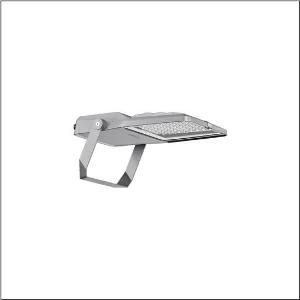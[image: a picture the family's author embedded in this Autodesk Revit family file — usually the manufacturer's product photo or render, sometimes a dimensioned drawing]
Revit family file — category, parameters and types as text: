
# Revit family: floodlight_fl_21_mini___pl33t_5xa7775c2f1a_de84
name_source: partatom
category: Lighting Fixtures
units: mm (PartAtom-declared; Revit-internal decimal feet)

## family parameters
Cut with Voids When Loaded = No
Host = Face
Light Source = No
Part Type = Normal
Room Calculation Point = No
Round Connector Dimension = Use Diameter
Shared = No

## types (1)
- --- (1 x LED, 12050 lm, 89 W, 3000K)
    Apparent Load = 89 VA
    CIE Flux Codes = 26 75 99 100 100
    Color Rendering = 70
    Color Temperature = 3000K
    Default Elevation = 1800 mm
    Description = Floodlight FL 21 mini, floodlight, primary light control with lens, of PMMA, primary optical cover: protective disc, of toughened safety glass, transparent, light distribution: PL33T, light emission: direct distribution, installation type: surface-mounted, LED, High Power LED, rated luminous flux: 12.050lm, luminous efficacy: 135lm/W, light colour: 730, colour temperature: 3000K, control: flexible luminous flux parameterisation, time-dependent luminous flux control, constant luminous flux control, overheat protection, presetting dimming logarithmic, with terminal, 6-pole, mains connection: 220..240V, AC, 50/60Hz, start of lifetime: 89W, end of service life: 94W, reduction: 43W, luminaire housing, of diecast aluminium, powder-coated, Siteco® metallic grey (DB 702S), corrosivity category C5 mid according to DIN EN ISO 12944, sealing non-destructively replaceable, mounting bracket, of steel, galvanised, powder-coated, Siteco® metallic grey (DB 702S), Smart Interface above, protection rating (complete): IP66, insulation class (complete): insulation class II (safety insulation), certification: CE, ENEC, VDE, protection symbol: D, impact resistance: IK08, permissible operating ambient temperature: -40..+40°C, permissible operating ambient temperature for outdoor applications: -40..+50°C, standard: DIN EN 12944, LABS conformity tested according to VDMA 24364:2018-05, packaging unit: 1 piece

Light Distribution: PL33T
    Height = 70 mm
    Lamp = 1 x LED
    Lamp Light Flux = 12050 lm
    Lamp Power = 89 W
    Lamp count = 1
    Length = 485 mm
    Luminous efficacy = 135 lm/W
    Manufacturer = Siteco
    ModVariant = No
    Model = 5XA7775C2F1A
    Number of Poles = 1
    OnlyDefault = Yes
    Power Factor = 1
    Product Name = Floodlight FL 21 mini | PL33T
    Product group = floodlight | pylon annexe
    ProductGroupID = 6200
    Protection Class = Protection class II
    Protection Degree = IP 66
    RLX_Detail_Level = 1
    RLX_Emergency_Light_Flux = 0 lm
    RLX_Emergency_Type = 0
    RLX_Emergency_Type_DB = No
    RlxData = <blob elided: 95901 chars, md5=86abb09b>
    Socket = socket
    Standby Power = 0 W
    System Light Flux = 12050 lm
    System Power = 89 W
    Type Comments = factory setting: luminous flux: 100 % | dim-lin: 254 | 456 mA
    Type Image = l_1006845.jpg
    URL = http://relux.com
    VarID = @adj_081057
    Voltage = 0 V
    Weight = 0.00 kg
    Width = 337 mm

## geometry (parser evidence)
native form markers: Blend x4, Sweep x12
no freeform markers — native parametric forms only
